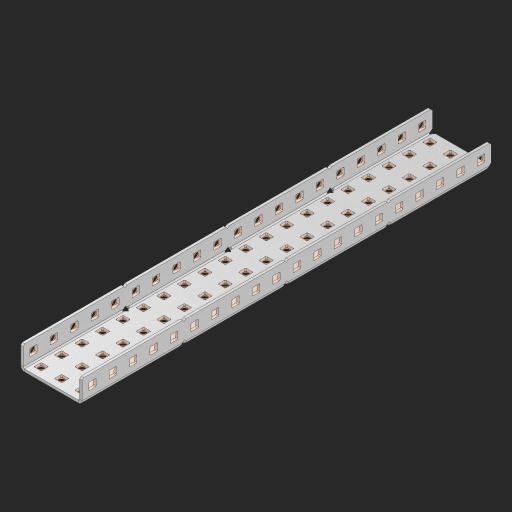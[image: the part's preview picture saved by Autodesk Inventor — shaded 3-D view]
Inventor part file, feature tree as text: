
AUTODESK INVENTOR PART (.ipt)
format: ipt  version: 2023 (Build 270158000, 158)  size: 1,366,528 bytes
history: native  units: in
note: dims shown in document units (in); Inventor stores cm internally (conversion verified against a paired STEP export)
features: other x105, extrude x99, sheet_metal_op x10, sketch x8, mirror x1, pattern_linear x1, chamfer x1
ambient origin geometry x8: Origin, YZ Plane, XZ Plane, XY Plane, X Axis, Y Axis, Z Axis, Center Point
bodies: Solid1 (feature_tree), Body (feature_tree)
feature tree (225):
  other  "Flange Pattern Plane"
  sheet_metal_op  "Flange Pattern"
  sheet_metal_op  "Body Pattern"
  other  "Arc Length"
  mirror  "Notch Mirror"
  pattern_linear  "Notch Pattern"  Spacing1=0.25in  [1 undecoded]
  chamfer  "End Chamfer"
  extrude  "Half Cut"  Depth=0.0625in
  sketch  "Sketch1"  dims[d0=1.5in]
  other  "Plate1"
  sketch  "Sketch2"  dims[d1=10.0in]
  other  "Plate2"
  sheet_metal_op  "Bend1"
  sheet_metal_op  "Corner1"
  sketch  "Sketch3"  dims[d2=0.0625in]
  other  "Flange Pattern Sketch"
  sketch  "Sketch7"  dims[d3=0.0625in]
  other  "Srf1"
  other  "Srf2"
  sketch  "Sketch8"  dims[d4=0.0312in]
  sketch  "Sketch9"  dims[d5=0.125in]
  other  "Srf91"
  sheet_metal_op  "Body Pattern Sketch"
  other  "Srf92"
  sketch  "Sketch13"  dims[d6=0.0625in]
  sketch  "Sketch14"  dims[d7=0.5in d8=90.0deg d9=0.0312in d10=0.25in d11=0.0625in d12=0.0625in d16=0.182in d17=0.02in d18=0.0625in d19=0.0in d20=0.25in d21=0.25in d46=0.172in d47=1.0in d48=0.0in d49=0.182in d50=0.02in d51=0.25in d52=0.25in d53=0.0625in d54=0.0in d55=0.172in d56=1.0in d57=0.0in d60=7.874in d62=0.5in d63=1.1811in d65=0.5in d85=0.1473in d86=0.1782in d88=0.04in d89=0.0625in d90=0.0in d91=0.04in d92=0.0491in d95=2.5in d96=0.04in d97=0.25in d98=45.0deg d101=0.0in d102=2.497in d131=1.5in d132=7.874in d134=0.5in d139=0.5in]
  other  "Srf856"
  other  "Srf1310"
  other  "Srf1311"
  other  "Srf1312"
  other  "Srf1376"
  other  "Srf1377"
  other  "Srf1728"
  other  "Srf1755"
  other  "Srf1878"
  other  "Srf1879"
  other  "Srf1880"
  other  "Srf1881"
  other  "Srf1882"
  other  "Srf1883"
  other  "Srf1884"
  other  "Srf1885"
  other  "Srf1886"
  other  "Srf1887"
  other  "Srf1888"
  other  "Srf1889"
  other  "Srf1890"
  other  "Srf1891"
  other  "Srf1892"
  other  "Srf1893"
  other  "Srf1894"
  other  "Srf1895"
  other  "Srf1896"
  other  "Srf1897"
  other  "Srf1898"
  other  "Srf1899"
  other  "Srf1900"
  other  "Srf1901"
  other  "Srf1902"
  other  "Srf1903"
  other  "Srf1904"
  other  "Srf1905"
  other  "Srf1906"
  other  "Srf1907"
  other  "Srf1908"
  other  "Srf1909"
  other  "Srf1910"
  other  "Srf1911"
  other  "Srf1942"
  other  "Srf1943"
  other  "Srf1944"
  other  "Srf1945"
  other  "Srf1946"
  other  "Srf1947"
  other  "Srf1948"
  other  "Srf1949"
  other  "Srf1950"
  other  "Srf1951"
  other  "Srf1952"
  other  "Srf1953"
  other  "Srf1954"
  other  "Srf1955"
  other  "Srf1956"
  other  "Srf1957"
  other  "Srf1958"
  other  "Srf1959"
  other  "Srf1960"
  other  "Srf1961"
  other  "Srf1962"
  other  "Srf1963"
  other  "Srf1964"
  other  "Srf1965"
  other  "Srf1966"
  other  "Srf1967"
  other  "Srf1968"
  other  "Srf1969"
  other  "Srf1970"
  other  "Srf1971"
  other  "Srf1972"
  other  "Srf1973"
  other  "Srf1974"
  other  "Srf1975"
  other  "Srf1976"
  other  "Srf1977"
  other  "Srf1978"
  other  "Srf1979"
  other  "Srf1980"
  other  "Srf1981"
  other  "Srf1982"
  other  "Srf1983"
  other  "Srf1984"
  other  "Srf1985"
  other  "Srf1986"
  other  "Srf1987"
  other  "Srf1988"
  other  "Srf1989"
  other  "Srf1990"
  other  "Srf1991"
  other  "Srf1992"
  other  "Srf1993"
  other  "Srf1994"
  other  "Srf1995"
  sheet_metal_op  "Flange Stamp"
  sheet_metal_op  "Flange Circle"
  sheet_metal_op  "Body Stamp"
  sheet_metal_op  "Body Circle"
  sheet_metal_op  "Notch"
  extrude  "ExtrusionSrf2"  Depth=0.0625in
  extrude  "ExtrusionSrf92"  Depth=1.5in
  extrude  "ExtrusionSrf856"  Depth=0.02in
  extrude  "ExtrusionSrf1310"  Depth=0.0625in
  extrude  "ExtrusionSrf1311"  TaperAngle=0.0deg  [1 undecoded]
  extrude  "ExtrusionSrf1312"  Depth=0.25in
  extrude  "ExtrusionSrf1376"  Depth=0.25in
  extrude  "ExtrusionSrf1377"  Depth=1.5in
  extrude  "ExtrusionSrf1728"  Depth=1.5in TaperAngle=0.0deg
  extrude  "ExtrusionSrf1755"  Depth=1.5in
  extrude  "ExtrusionSrf1878"  Depth=0.02in
  extrude  "ExtrusionSrf1879"  Depth=0.25in
  extrude  "ExtrusionSrf1880"  Depth=0.25in
  extrude  "ExtrusionSrf1881"  Depth=0.0625in
  extrude  "ExtrusionSrf1882"  TaperAngle=0.0deg  [1 undecoded]
  extrude  "ExtrusionSrf1883"  Depth=1.5in
  extrude  "ExtrusionSrf1884"  Depth=1.5in TaperAngle=0.0deg
  extrude  "ExtrusionSrf1885"  Depth=1.5in
  extrude  "ExtrusionSrf1886"  Depth=1.5in
  extrude  "ExtrusionSrf1887"  Depth=1.5in
  extrude  "ExtrusionSrf1888"  Depth=1.5in
  extrude  "ExtrusionSrf1889"  Depth=1.5in
  extrude  "ExtrusionSrf1890"  Depth=0.0625in
  extrude  "ExtrusionSrf1891"  TaperAngle=0.0deg  [1 undecoded]
  extrude  "ExtrusionSrf1892"  Depth=1.5in
  extrude  "ExtrusionSrf1893"  Depth=1.5in
  extrude  "ExtrusionSrf1894"  Depth=1.5in
  extrude  "ExtrusionSrf1895"  Depth=0.25in TaperAngle=45.0deg
  extrude  "ExtrusionSrf1896"  TaperAngle=0.0deg  [1 undecoded]
  extrude  "ExtrusionSrf1897"  Depth=1.5in
  extrude  "ExtrusionSrf1898"  Depth=1.5in
  extrude  "ExtrusionSrf1899"  Depth=1.5in
  extrude  "ExtrusionSrf1900"  Depth=1.5in
  extrude  "ExtrusionSrf1901"  Depth=1.5in
  extrude  "ExtrusionSrf1902"  [1 undecoded]
  extrude  "ExtrusionSrf1903"  [1 undecoded]
  extrude  "ExtrusionSrf1904"  [1 undecoded]
  extrude  "ExtrusionSrf1905"  [1 undecoded]
  extrude  "ExtrusionSrf1906"  [1 undecoded]
  extrude  "ExtrusionSrf1907"  [1 undecoded]
  extrude  "ExtrusionSrf1908"  [1 undecoded]
  extrude  "ExtrusionSrf1909"  [1 undecoded]
  extrude  "ExtrusionSrf1910"  [1 undecoded]
  extrude  "ExtrusionSrf1911"  [1 undecoded]
  extrude  "ExtrusionSrf1942"  [1 undecoded]
  extrude  "ExtrusionSrf1943"  [1 undecoded]
  extrude  "ExtrusionSrf1944"  [1 undecoded]
  extrude  "ExtrusionSrf1945"  [1 undecoded]
  extrude  "ExtrusionSrf1946"  [1 undecoded]
  extrude  "ExtrusionSrf1947"  [1 undecoded]
  extrude  "ExtrusionSrf1948"  [1 undecoded]
  extrude  "ExtrusionSrf1949"  [1 undecoded]
  extrude  "ExtrusionSrf1950"  [1 undecoded]
  extrude  "ExtrusionSrf1951"  [1 undecoded]
  extrude  "ExtrusionSrf1952"  [1 undecoded]
  extrude  "ExtrusionSrf1953"  [1 undecoded]
  extrude  "ExtrusionSrf1954"  [1 undecoded]
  extrude  "ExtrusionSrf1955"  [1 undecoded]
  extrude  "ExtrusionSrf1956"  [1 undecoded]
  extrude  "ExtrusionSrf1957"  [1 undecoded]
  extrude  "ExtrusionSrf1958"  [1 undecoded]
  extrude  "ExtrusionSrf1959"  [1 undecoded]
  extrude  "ExtrusionSrf1960"  [1 undecoded]
  extrude  "ExtrusionSrf1961"  [1 undecoded]
  extrude  "ExtrusionSrf1962"  [1 undecoded]
  extrude  "ExtrusionSrf1963"  [1 undecoded]
  extrude  "ExtrusionSrf1964"  [1 undecoded]
  extrude  "ExtrusionSrf1965"  [1 undecoded]
  extrude  "ExtrusionSrf1966"  [1 undecoded]
  extrude  "ExtrusionSrf1967"  [1 undecoded]
  extrude  "ExtrusionSrf1968"  [1 undecoded]
  extrude  "ExtrusionSrf1969"  [1 undecoded]
  extrude  "ExtrusionSrf1970"  [1 undecoded]
  extrude  "ExtrusionSrf1971"  [1 undecoded]
  extrude  "ExtrusionSrf1972"  [1 undecoded]
  extrude  "ExtrusionSrf1973"  [1 undecoded]
  extrude  "ExtrusionSrf1974"  [1 undecoded]
  extrude  "ExtrusionSrf1975"  [1 undecoded]
  extrude  "ExtrusionSrf1976"  [1 undecoded]
  extrude  "ExtrusionSrf1977"  [1 undecoded]
  extrude  "ExtrusionSrf1978"  [1 undecoded]
  extrude  "ExtrusionSrf1979"  [1 undecoded]
  extrude  "ExtrusionSrf1980"  [1 undecoded]
  extrude  "ExtrusionSrf1981"  [1 undecoded]
  extrude  "ExtrusionSrf1982"  [1 undecoded]
  extrude  "ExtrusionSrf1983"  [1 undecoded]
  extrude  "ExtrusionSrf1984"  [1 undecoded]
  extrude  "ExtrusionSrf1985"  [1 undecoded]
  extrude  "ExtrusionSrf1986"  [1 undecoded]
  extrude  "ExtrusionSrf1987"  [1 undecoded]
  extrude  "ExtrusionSrf1988"  [1 undecoded]
  extrude  "ExtrusionSrf1989"  [1 undecoded]
  extrude  "ExtrusionSrf1990"  [1 undecoded]
  extrude  "ExtrusionSrf1991"  [1 undecoded]
  extrude  "ExtrusionSrf1992"  [1 undecoded]
  extrude  "ExtrusionSrf1993"  [1 undecoded]
  extrude  "ExtrusionSrf1994"  [1 undecoded]
  extrude  "ExtrusionSrf1995"  [1 undecoded]
note: 69 required parameter values undecoded (feature->parameter linkage not recoverable at this tier; creation-order binding heuristic only, values carry confidence <= 0.55)
